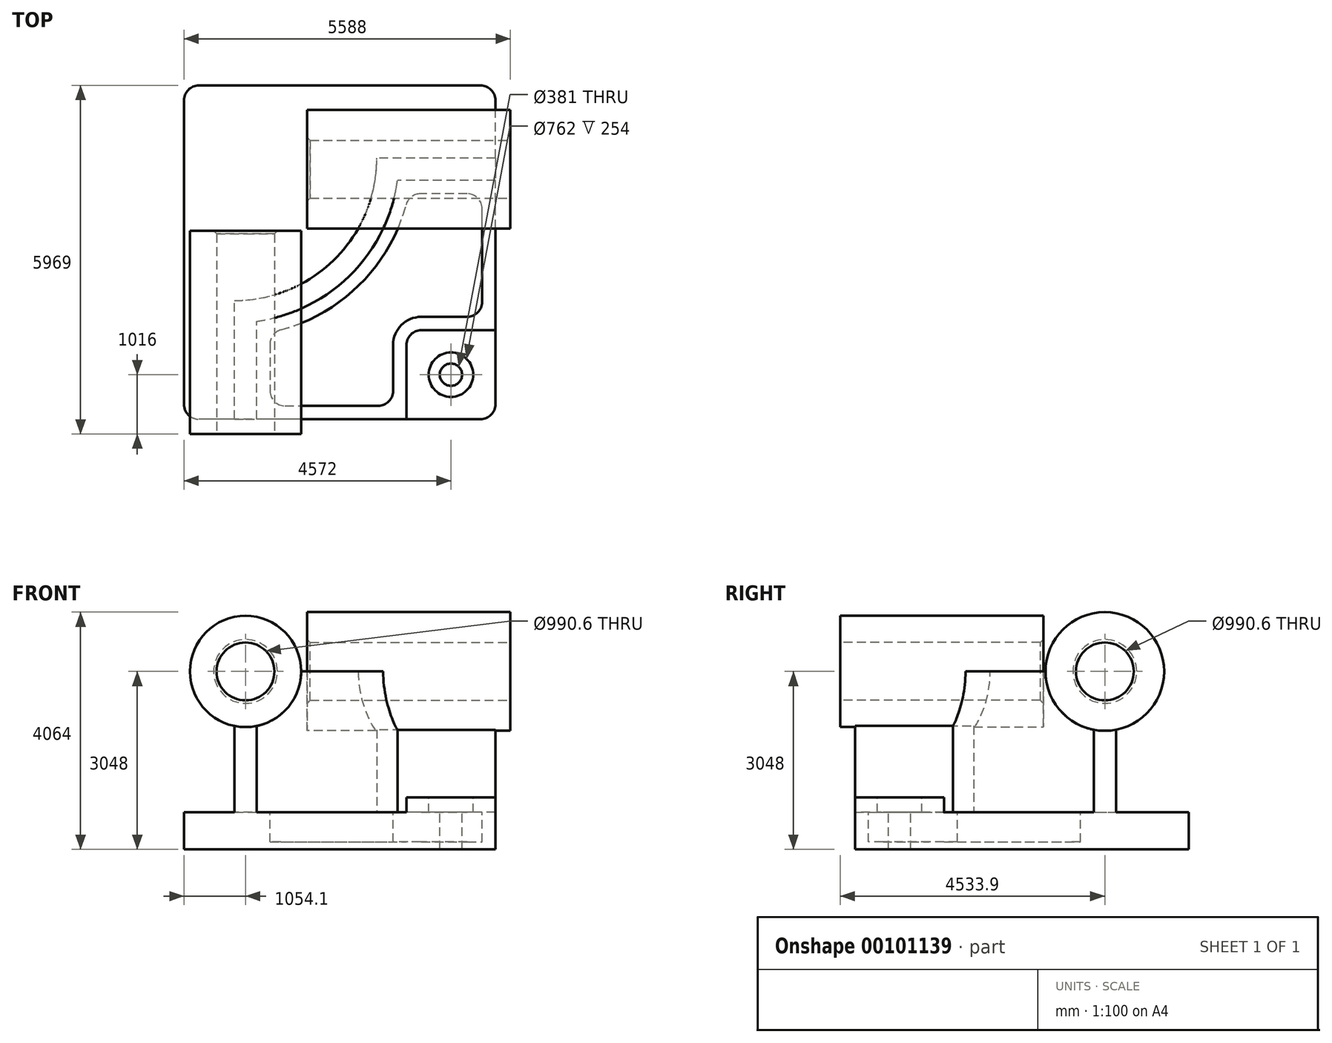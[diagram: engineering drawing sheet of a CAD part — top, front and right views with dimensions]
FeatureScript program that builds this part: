
annotation { "Feature Type Name" : "Feature", "Feature Type Description" : "" }
export const myFeature = defineFeature(function(context is Context, id is Id, definition is map)
    precondition{}
    {
        {
            var Q0;
            Q0=qCreatedBy(makeId("Top.planeOp"),FACE);
            var sketch = newSketch(context, id + "F0", { "sketchPlane" : qUnion([Q0])});
            skLineSegment(sketch, "E0.bottom", {"start": v(2667, -2857.5) * mm, "end": v(-2667, -2857.5) * mm});
            skLineSegment(sketch, "E0.top", {"start": v(2667, 2857.5) * mm, "end": v(-2667, 2857.5) * mm});
            skLineSegment(sketch, "E0.left", {"start": v(2667, -2857.5) * mm, "end": v(2667, 2857.5) * mm});
            skLineSegment(sketch, "E0.right", {"start": v(-2667, -2857.5) * mm, "end": v(-2667, 2857.5) * mm});
            skPoint(sketch, "E0.middle", {"position": v(0, 0) * mm});
            skSolve(sketch);
        }
        {
            var Q0;
            Q0=makeQuery(id+"F0.imprint","IMPRINT",FACE,{"disambiguationData":[TD([[makeQuery(id+"F0.imprint","IMPRINT",EDGE,{"derivedFrom":sQuery(id+"F0.wireOp",EDGE,"E0.bottom")}),-1.0]])]});
            extrude(context, id + "F1", {"entities" : qUnion([Q0]), "depth" : 635 * mm});
        }
        {
            var Q0;
            Q0=makeQuery(id+"F1.opExtrude","CAP_FACE",FACE,{"disambiguationData":[OSD([sQuery(id+"F0.wireOp",EDGE,"E0.bottom"),sQuery(id+"F0.wireOp",EDGE,"E0.top"),sQuery(id+"F0.wireOp",EDGE,"E0.left"),sQuery(id+"F0.wireOp",EDGE,"E0.right")])],"isStart":false});
            var sketch = newSketch(context, id + "F2", { "sketchPlane" : qUnion([Q0])});
            skLineSegment(sketch, "E1", {"start": v(-1803.4, -2857.5) * mm, "end": v(-1803.4, -825.5) * mm});
            skLineSegment(sketch, "E2", {"start": v(2667, 1612.9) * mm, "end": v(635, 1612.9) * mm});
            skArc(sketch, "E3", {"start": v(-1803.4, -825.5) * mm, "mid": v(-79.2, -111.3) * mm, "end": v(635, 1612.9) * mm});
            skLineSegment(sketch, "E4", {"start": v(-1803.4, 1612.9) * mm, "end": v(635, 1612.9) * mm, "construction": true});
            skLineSegment(sketch, "E5", {"start": v(-1803.4, 1612.9) * mm, "end": v(-1803.4, -825.5) * mm, "construction": true});
            skLineSegment(sketch, "E6.0", {"start": v(-1422.4, -2857.5) * mm, "end": v(-1422.4, -1180.64) * mm});
            skArc(sketch, "E6.1", {"start": v(-1422.4, -1180.64) * mm, "mid": v(190.22, -380.72) * mm, "end": v(990.14, 1231.9) * mm});
            skLineSegment(sketch, "E6.2", {"start": v(2667, 1231.9) * mm, "end": v(990.14, 1231.9) * mm});
            skLineSegment(sketch, "E7.0", {"start": v(2667, -2857.5) * mm, "end": v(2667, 2857.5) * mm});
            skLineSegment(sketch, "E8.0", {"start": v(2667, -2857.5) * mm, "end": v(-2667, -2857.5) * mm});
            skSolve(sketch);
        }
        {
            var Q0;
            {var subQ2=sQuery(id+"F2.wireOp",EDGE,"E1");Q0=makeQuery(id+"F2.imprint","IMPRINT",FACE,{"disambiguationData":[TD([[makeQuery(id+"F2.imprint","IMPRINT",EDGE,{"derivedFrom":subQ2}),-1.0]])]});}
            extrude(context, id + "F3", {"entities" : qUnion([Q0]), "operationType" : NewBodyOperationType.ADD, "depth" : 2413 * mm});
        }
        {
            var Q0;
            Q0=makeQuery(id+"F3.boolean.opBoolean","MERGE",FACE,{"derivedFrom":[makeQuery(id+"F1.opExtrude","SWEPT_FACE",FACE,{"disambiguationData":[OSD([sQuery(id+"F0.wireOp",EDGE,"E0.bottom")])]}),makeQuery(id+"F3.opExtrude","SWEPT_FACE",FACE,{"disambiguationData":[OSD([sQuery(id+"F2.wireOp",EDGE,"E8.0")])]})]});
            var sketch = newSketch(context, id + "F4", { "sketchPlane" : qUnion([Q0])});
            skCircle(sketch, "E9", {"center": v(-1612.9, 3048) * mm, "radius": 952.5 * mm});
            skSolve(sketch);
        }
        {
            var Q0;
            Q0 = qSketchRegion(id + "F4", true);
            extrude(context, id + "F5", {"entities" : qUnion([Q0]), "operationType" : NewBodyOperationType.ADD, "depth" : 254 * mm, "hasSecondDirection" : true, "secondDirectionOppositeDirection" : true, "secondDirectionDepth" : 3225.8 * mm});
        }
        {
            var Q0;
            Q0=makeQuery(id+"F3.boolean.opBoolean","MERGE",FACE,{"derivedFrom":[makeQuery(id+"F1.opExtrude","SWEPT_FACE",FACE,{"disambiguationData":[OSD([sQuery(id+"F0.wireOp",EDGE,"E0.left")])]}),makeQuery(id+"F3.opExtrude","SWEPT_FACE",FACE,{"disambiguationData":[OSD([sQuery(id+"F2.wireOp",EDGE,"E7.0")])]})]});
            var sketch = newSketch(context, id + "F6", { "sketchPlane" : qUnion([Q0])});
            skCircle(sketch, "E10", {"center": v(1422.4, 3048) * mm, "radius": 1016 * mm});
            skSolve(sketch);
        }
        {
            var Q0;
            Q0 = qSketchRegion(id + "F6", true);
            extrude(context, id + "F7", {"entities" : qUnion([Q0]), "operationType" : NewBodyOperationType.ADD, "depth" : 254 * mm, "hasSecondDirection" : true, "secondDirectionOppositeDirection" : true, "secondDirectionDepth" : 3225.8 * mm});
        }
        {
            var Q0;
            {var subQ0=sQuery(id+"F0.wireOp",EDGE,"E0.left");var subQ1=sQuery(id+"F0.wireOp",EDGE,"E0.bottom");Q0=makeQuery(id+"F3.boolean.opBoolean","SPLIT",FACE,{"disambiguationData":[TD([makeQuery(id+"F3.opExtrude","SWEPT_FACE",FACE,{"disambiguationData":[OSD([sQuery(id+"F2.wireOp",EDGE,"E6.0")])]})])],"derivedFrom":makeQuery(id+"F1.opExtrude","CAP_FACE",FACE,{"disambiguationData":[OSD([subQ1,sQuery(id+"F0.wireOp",EDGE,"E0.top"),subQ0,sQuery(id+"F0.wireOp",EDGE,"E0.right")])],"isStart":false})});}
            var sketch = newSketch(context, id + "F8", { "sketchPlane" : qUnion([Q0])});
            skLineSegment(sketch, "E11.bottom", {"start": v(2667, -2857.5) * mm, "end": v(1143, -2857.5) * mm});
            skLineSegment(sketch, "E11.top", {"start": v(2667, -1333.5) * mm, "end": v(1143, -1333.5) * mm});
            skLineSegment(sketch, "E11.left", {"start": v(2667, -2857.5) * mm, "end": v(2667, -1333.5) * mm});
            skLineSegment(sketch, "E11.right", {"start": v(1143, -2857.5) * mm, "end": v(1143, -1333.5) * mm});
            skSolve(sketch);
        }
        {
            var Q0;
            Q0 = qSketchRegion(id + "F8", true);
            extrude(context, id + "F9", {"entities" : qUnion([Q0]), "operationType" : NewBodyOperationType.ADD, "depth" : 254 * mm});
        }
        {
            var Q0;
            Q0=makeQuery(id+"F9.opExtrude","SWEPT_EDGE",EDGE,{"disambiguationData":[OSD([sQuery(id+"F8.wireOp",EDGE,"E11.top"),sQuery(id+"F8.wireOp",EDGE,"E11.right")])]});
            fillet(context, id + "F10", {"entities" : qUnion([Q0]), "radius" : 254 * mm, "tangentPropagation" : true, "allowEdgeOverflow" : false});
        }
        {
            var Q0;
            {var subQ0=sQuery(id+"F0.wireOp",EDGE,"E0.left");var subQ1=sQuery(id+"F0.wireOp",EDGE,"E0.bottom");Q0=makeQuery(id+"F3.boolean.opBoolean","SPLIT",FACE,{"disambiguationData":[TD([makeQuery(id+"F3.opExtrude","SWEPT_FACE",FACE,{"disambiguationData":[OSD([sQuery(id+"F2.wireOp",EDGE,"E6.0")])]})])],"derivedFrom":makeQuery(id+"F1.opExtrude","CAP_FACE",FACE,{"disambiguationData":[OSD([subQ1,sQuery(id+"F0.wireOp",EDGE,"E0.top"),subQ0,sQuery(id+"F0.wireOp",EDGE,"E0.right")])],"isStart":false})});}
            var sketch = newSketch(context, id + "F11", { "sketchPlane" : qUnion([Q0])});
            skLineSegment(sketch, "E12.0", {"start": v(-1193.8, -1373.52) * mm, "end": v(-1193.8, -2628.9) * mm});
            skArc(sketch, "E12.1", {"start": v(1183.02, 1003.3) * mm, "mid": v(351.86, -542.36) * mm, "end": v(-1193.8, -1373.52) * mm});
            skLineSegment(sketch, "E12.2", {"start": v(-1193.8, -2628.9) * mm, "end": v(914.4, -2628.9) * mm});
            skLineSegment(sketch, "E12.3", {"start": v(2438.4, 1003.3) * mm, "end": v(1183.02, 1003.3) * mm});
            skLineSegment(sketch, "E12.4", {"start": v(914.4, -2628.9) * mm, "end": v(914.4, -1587.5) * mm});
            skArc(sketch, "E12.5", {"start": v(914.4, -1587.5) * mm, "mid": v(1055.75, -1246.25) * mm, "end": v(1397, -1104.9) * mm});
            skLineSegment(sketch, "E12.6", {"start": v(1397, -1104.9) * mm, "end": v(2438.4, -1104.9) * mm});
            skLineSegment(sketch, "E12.7", {"start": v(2438.4, -1104.9) * mm, "end": v(2438.4, 1003.3) * mm});
            skSolve(sketch);
        }
        {
            var Q0;
            Q0=makeQuery(id+"F11.imprint","IMPRINT",FACE,{"disambiguationData":[TD([[makeQuery(id+"F11.imprint","IMPRINT",EDGE,{"derivedFrom":sQuery(id+"F11.wireOp",EDGE,"E12.0")}),1.0]])]});
            extrude(context, id + "F12", {"entities" : qUnion([Q0]), "operationType" : NewBodyOperationType.REMOVE, "oppositeDirection" : true, "depth" : 508 * mm});
        }
        {
            var Q0;
            Q0=makeQuery(id+"F9.opExtrude","CAP_FACE",FACE,{"disambiguationData":[OSD([sQuery(id+"F8.wireOp",EDGE,"E11.bottom"),sQuery(id+"F8.wireOp",EDGE,"E11.top"),sQuery(id+"F8.wireOp",EDGE,"E11.left"),sQuery(id+"F8.wireOp",EDGE,"E11.right")])],"isStart":false});
            var sketch = newSketch(context, id + "F13", { "sketchPlane" : qUnion([Q0])});
            skCircle(sketch, "E13", {"center": v(1905, -2095.5) * mm, "radius": 381 * mm});
            skSolve(sketch);
        }
        {
            var Q0;
            Q0=sQuery(id+"F13.wireOp",VERTEX,"E13.center");
            var Q1;
            Q1=makeQuery(id+"F1.opExtrude","SWEPT_BODY",BODY,{"disambiguationData":[OSD([sQuery(id+"F0.wireOp",EDGE,"E0.bottom"),sQuery(id+"F0.wireOp",EDGE,"E0.top"),sQuery(id+"F0.wireOp",EDGE,"E0.left"),sQuery(id+"F0.wireOp",EDGE,"E0.right")])]});
            hole(context, id + "F14", {"style" : HoleStyle.C_BORE, "endStyle" : HoleEndStyle.THROUGH, "holeDiameter" : 381 * mm, "cBoreDiameter" : 762 * mm, "cBoreDepth" : 254 * mm, "tappedDepth" : 12.7 * mm, "tapClearance" : 3, "locations" : qUnion([Q0]), "scope" : qUnion([Q1])});
        }
        {
            var Q0;
            Q0=makeQuery(id+"F12.boolean.opBoolean","COPY",EDGE,{"derivedFrom":makeQuery(id+"F12.opExtrude","SWEPT_EDGE",EDGE,{"disambiguationData":[OSD([sQuery(id+"F11.wireOp",EDGE,"E12.0"),sQuery(id+"F11.wireOp",EDGE,"E12.1")])]})});
            var Q1;
            Q1=makeQuery(id+"F12.boolean.opBoolean","COPY",EDGE,{"derivedFrom":makeQuery(id+"F12.opExtrude","SWEPT_EDGE",EDGE,{"disambiguationData":[OSD([sQuery(id+"F11.wireOp",EDGE,"E12.1"),sQuery(id+"F11.wireOp",EDGE,"E12.3")])]})});
            var Q2;
            Q2=makeQuery(id+"F12.boolean.opBoolean","COPY",EDGE,{"derivedFrom":makeQuery(id+"F12.opExtrude","SWEPT_EDGE",EDGE,{"disambiguationData":[OSD([sQuery(id+"F11.wireOp",EDGE,"E12.3"),sQuery(id+"F11.wireOp",EDGE,"E12.7")])]})});
            var Q3;
            Q3=makeQuery(id+"F12.boolean.opBoolean","COPY",EDGE,{"derivedFrom":makeQuery(id+"F12.opExtrude","SWEPT_EDGE",EDGE,{"disambiguationData":[OSD([sQuery(id+"F11.wireOp",EDGE,"E12.6"),sQuery(id+"F11.wireOp",EDGE,"E12.7")])]})});
            var Q4;
            Q4=makeQuery(id+"F12.boolean.opBoolean","COPY",EDGE,{"derivedFrom":makeQuery(id+"F12.opExtrude","SWEPT_EDGE",EDGE,{"disambiguationData":[OSD([sQuery(id+"F11.wireOp",EDGE,"E12.2"),sQuery(id+"F11.wireOp",EDGE,"E12.4")])]})});
            var Q5;
            Q5=makeQuery(id+"F12.boolean.opBoolean","COPY",EDGE,{"derivedFrom":makeQuery(id+"F12.opExtrude","SWEPT_EDGE",EDGE,{"disambiguationData":[OSD([sQuery(id+"F11.wireOp",EDGE,"E12.0"),sQuery(id+"F11.wireOp",EDGE,"E12.2")])]})});
            fillet(context, id + "F15", {"entities" : qUnion([Q0, Q1, Q2, Q3, Q4, Q5]), "radius" : 254 * mm, "tangentPropagation" : true, "allowEdgeOverflow" : false});
        }
        {
            var Q0;
            Q0=makeQuery(id+"F5.opExtrude","CAP_FACE",FACE,{"disambiguationData":[OSD([sQuery(id+"F4.wireOp",EDGE,"E9")])],"isStart":false});
            var sketch = newSketch(context, id + "F16", { "sketchPlane" : qUnion([Q0])});
            skCircle(sketch, "E14", {"center": v(-1612.9, 3048) * mm, "radius": 495.3 * mm});
            skSolve(sketch);
        }
        {
            var Q0;
            Q0 = qSketchRegion(id + "F16", true);
            extrude(context, id + "F17", {"entities" : qUnion([Q0]), "operationType" : NewBodyOperationType.REMOVE, "endBound" : BoundingType.THROUGH_ALL, "oppositeDirection" : true, "depth" : 25.4 * mm});
        }
        {
            var Q0;
            Q0=makeQuery(id+"F7.opExtrude","CAP_FACE",FACE,{"disambiguationData":[OSD([sQuery(id+"F6.wireOp",EDGE,"E10")])],"isStart":false});
            var sketch = newSketch(context, id + "F18", { "sketchPlane" : qUnion([Q0])});
            skCircle(sketch, "E15", {"center": v(1422.4, 3048) * mm, "radius": 495.3 * mm});
            skSolve(sketch);
        }
        {
            var Q0;
            Q0 = qSketchRegion(id + "F18", true);
            extrude(context, id + "F19", {"entities" : qUnion([Q0]), "operationType" : NewBodyOperationType.REMOVE, "endBound" : BoundingType.THROUGH_ALL, "oppositeDirection" : true, "depth" : 25.4 * mm});
        }
        {
            var Q0;
            Q0=makeQuery(id+"F17.boolean.opBoolean","COPY",EDGE,{"derivedFrom":makeQuery(id+"F17.opExtrude","CAP_EDGE",EDGE,{"disambiguationData":[OSD([sQuery(id+"F16.wireOp",EDGE,"E14")])],"isStart":true})});
            var Q1;
            Q1=makeQuery(id+"F19.boolean.opBoolean","COPY",EDGE,{"derivedFrom":makeQuery(id+"F19.opExtrude","CAP_EDGE",EDGE,{"disambiguationData":[OSD([sQuery(id+"F18.wireOp",EDGE,"E15")])],"isStart":true})});
            var Q2;
            Q2=makeQuery(id+"F17.boolean.opBoolean","INTERSECT",EDGE,{"derivedFrom":[makeQuery(id+"F5.opExtrude","CAP_FACE",FACE,{"disambiguationData":[OSD([sQuery(id+"F4.wireOp",EDGE,"E9")])],"isStart":true}),makeQuery(id+"F17.opExtrude","SWEPT_FACE",FACE,{"disambiguationData":[OSD([sQuery(id+"F16.wireOp",EDGE,"E14")])]})]});
            var Q3;
            Q3=makeQuery(id+"F19.boolean.opBoolean","INTERSECT",EDGE,{"derivedFrom":[makeQuery(id+"F7.opExtrude","CAP_FACE",FACE,{"disambiguationData":[OSD([sQuery(id+"F6.wireOp",EDGE,"E10")])],"isStart":true}),makeQuery(id+"F19.opExtrude","SWEPT_FACE",FACE,{"disambiguationData":[OSD([sQuery(id+"F18.wireOp",EDGE,"E15")])]})]});
            chamfer(context, id + "F20", {"entities" : qUnion([Q0, Q1, Q2, Q3]), "width" : 50.8 * mm, "tangentPropagation" : true});
        }
        {
            var Q0;
            Q0=makeQuery(id+"F1.opExtrude","SWEPT_EDGE",EDGE,{"disambiguationData":[OSD([sQuery(id+"F0.wireOp",EDGE,"E0.bottom"),sQuery(id+"F0.wireOp",EDGE,"E0.right")])]});
            var Q1;
            Q1=makeQuery(id+"F9.boolean.opBoolean","MERGE",EDGE,{"derivedFrom":[makeQuery(id+"F1.opExtrude","SWEPT_EDGE",EDGE,{"disambiguationData":[OSD([sQuery(id+"F0.wireOp",EDGE,"E0.bottom"),sQuery(id+"F0.wireOp",EDGE,"E0.left")])]}),makeQuery(id+"F9.opExtrude","SWEPT_EDGE",EDGE,{"disambiguationData":[OSD([sQuery(id+"F8.wireOp",EDGE,"E11.bottom"),sQuery(id+"F8.wireOp",EDGE,"E11.left")])]})]});
            var Q2;
            Q2=makeQuery(id+"F1.opExtrude","SWEPT_EDGE",EDGE,{"disambiguationData":[OSD([sQuery(id+"F0.wireOp",EDGE,"E0.top"),sQuery(id+"F0.wireOp",EDGE,"E0.left")])]});
            var Q3;
            Q3=makeQuery(id+"F1.opExtrude","SWEPT_EDGE",EDGE,{"disambiguationData":[OSD([sQuery(id+"F0.wireOp",EDGE,"E0.top"),sQuery(id+"F0.wireOp",EDGE,"E0.right")])]});
            fillet(context, id + "F21", {"entities" : qUnion([Q0, Q1, Q2, Q3]), "radius" : 254 * mm, "tangentPropagation" : true, "allowEdgeOverflow" : false});
        }
    });
